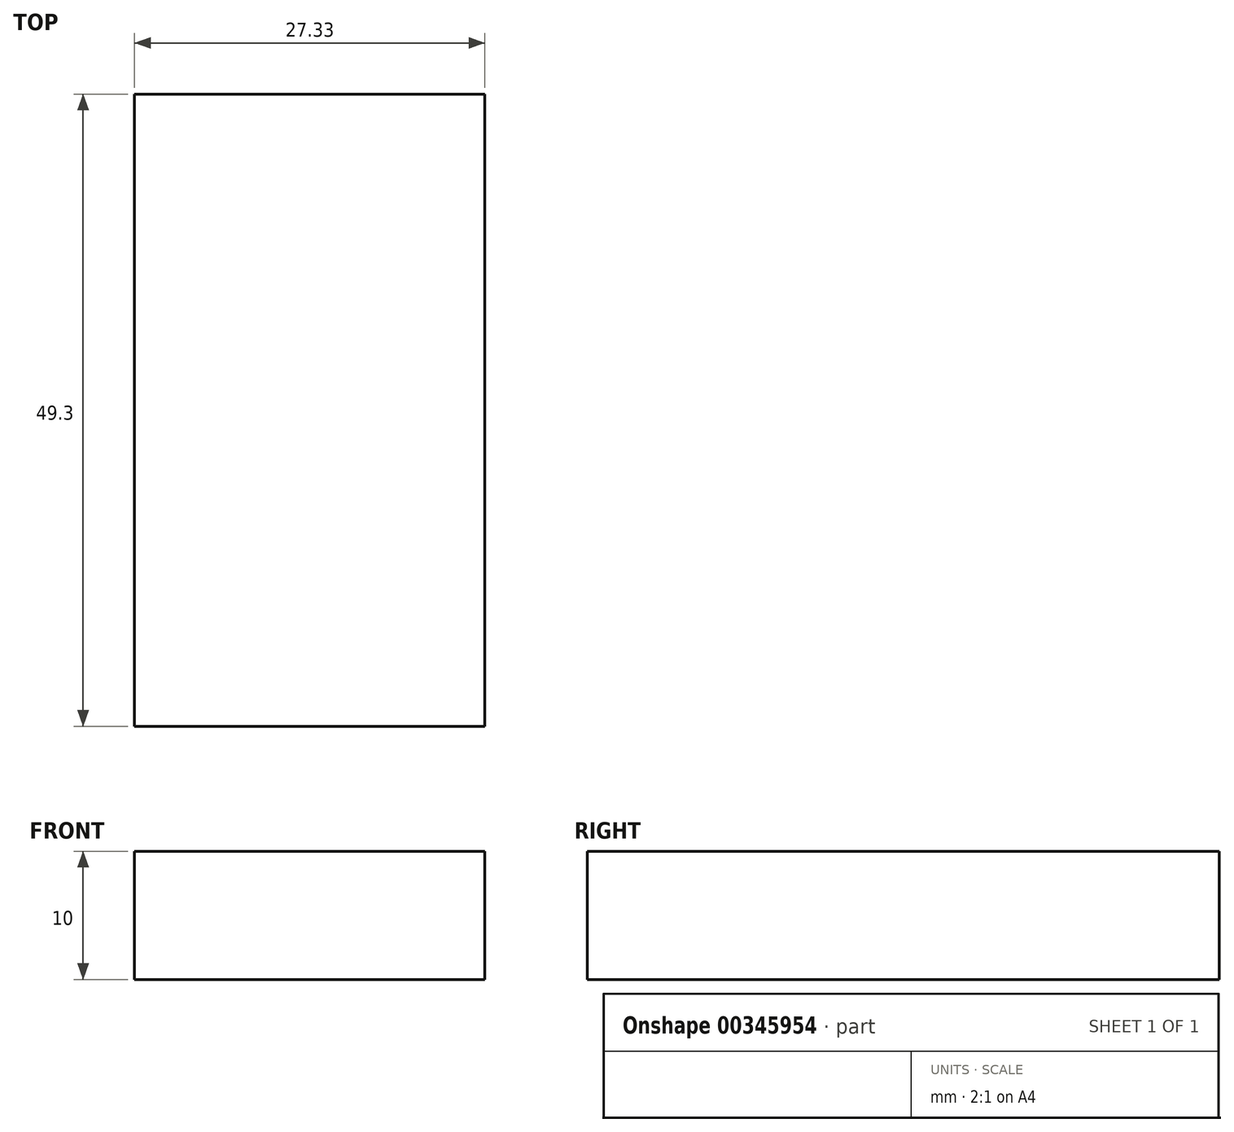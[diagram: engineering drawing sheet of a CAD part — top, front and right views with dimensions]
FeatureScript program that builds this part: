
annotation { "Feature Type Name" : "Feature", "Feature Type Description" : "" }
export const myFeature = defineFeature(function(context is Context, id is Id, definition is map)
    precondition{}
    {
        {
            var Q0;
            Q0=qCreatedBy(makeId("Top.planeOp"),FACE);
            var sketch = newSketch(context, id + "F0", { "sketchPlane" : qUnion([Q0])});
            skLineSegment(sketch, "E0.bottom", {"start": v(0, 0) * mm, "end": v(0, 0) * mm});
            skLineSegment(sketch, "E0.top", {"start": v(0, 0) * mm, "end": v(0, 0) * mm});
            skLineSegment(sketch, "E0.left", {"start": v(0, 0) * mm, "end": v(0, 0) * mm});
            skLineSegment(sketch, "E0.right", {"start": v(0, 0) * mm, "end": v(0, 0) * mm});
            skLineSegment(sketch, "E1.bottom", {"start": v(0, -49.3) * mm, "end": v(27.33, -49.3) * mm});
            skLineSegment(sketch, "E1.top", {"start": v(0, 0) * mm, "end": v(27.33, 0) * mm});
            skLineSegment(sketch, "E1.left", {"start": v(0, -49.3) * mm, "end": v(0, 0) * mm});
            skLineSegment(sketch, "E1.right", {"start": v(27.33, -49.3) * mm, "end": v(27.33, 0) * mm});
            skSolve(sketch);
        }
        {
            var Q0;
            Q0=makeQuery(id+"F0.imprint","IMPRINT",FACE,{"disambiguationData":[TD([[makeQuery(id+"F0.imprint","IMPRINT",EDGE,{"derivedFrom":sQuery(id+"F0.wireOp",EDGE,"E1.bottom")}),1.0]])]});
            var sketch = newSketch(context, id + "F1", { "sketchPlane" : qUnion([Q0])});
            skSolve(sketch);
        }
        {
            var Q0;
            Q0 = qSketchRegion(id + "F1", true);
            var Q1;
            Q1=makeQuery(id+"F1.imprint","IMPRINT",FACE,{"disambiguationData":[TD([[makeQuery(id+"F1.imprint","IMPRINT",EDGE,{"derivedFrom":makeQuery(id+"F0.imprint","IMPRINT",EDGE,{"derivedFrom":sQuery(id+"F0.wireOp",EDGE,"E1.bottom")})}),1.0]])]});
            extrude(context, id + "F2", {"entities" : qUnion([Q0, Q1]), "depth" : 10 * mm});
        }
    });
